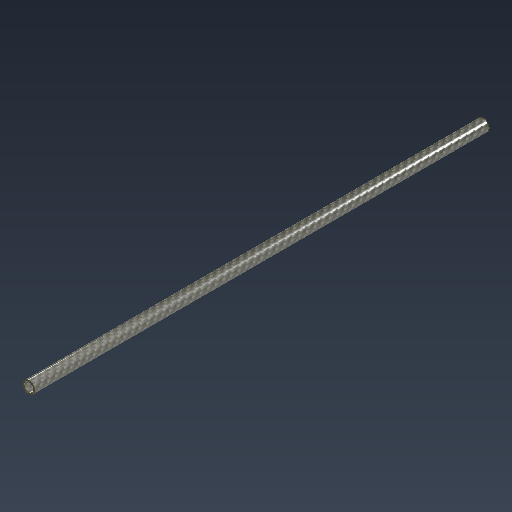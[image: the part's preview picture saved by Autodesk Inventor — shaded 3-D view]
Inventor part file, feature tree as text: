
AUTODESK INVENTOR PART (.ipt)
format: ipt  version: 2024.1 (Build 281209000, 209)  size: 113,152 bytes
history: native  units: mm
features: other x1, extrude x1
ambient origin geometry x8: Origin, YZ Plane, XZ Plane, XY Plane, X Axis, Y Axis, Z Axis, Center Point
bodies: Solid1 (feature_tree)
feature tree (2):
  other  "Loadpipe"
  extrude  "Extrusion1"  Depth=12.0mm
